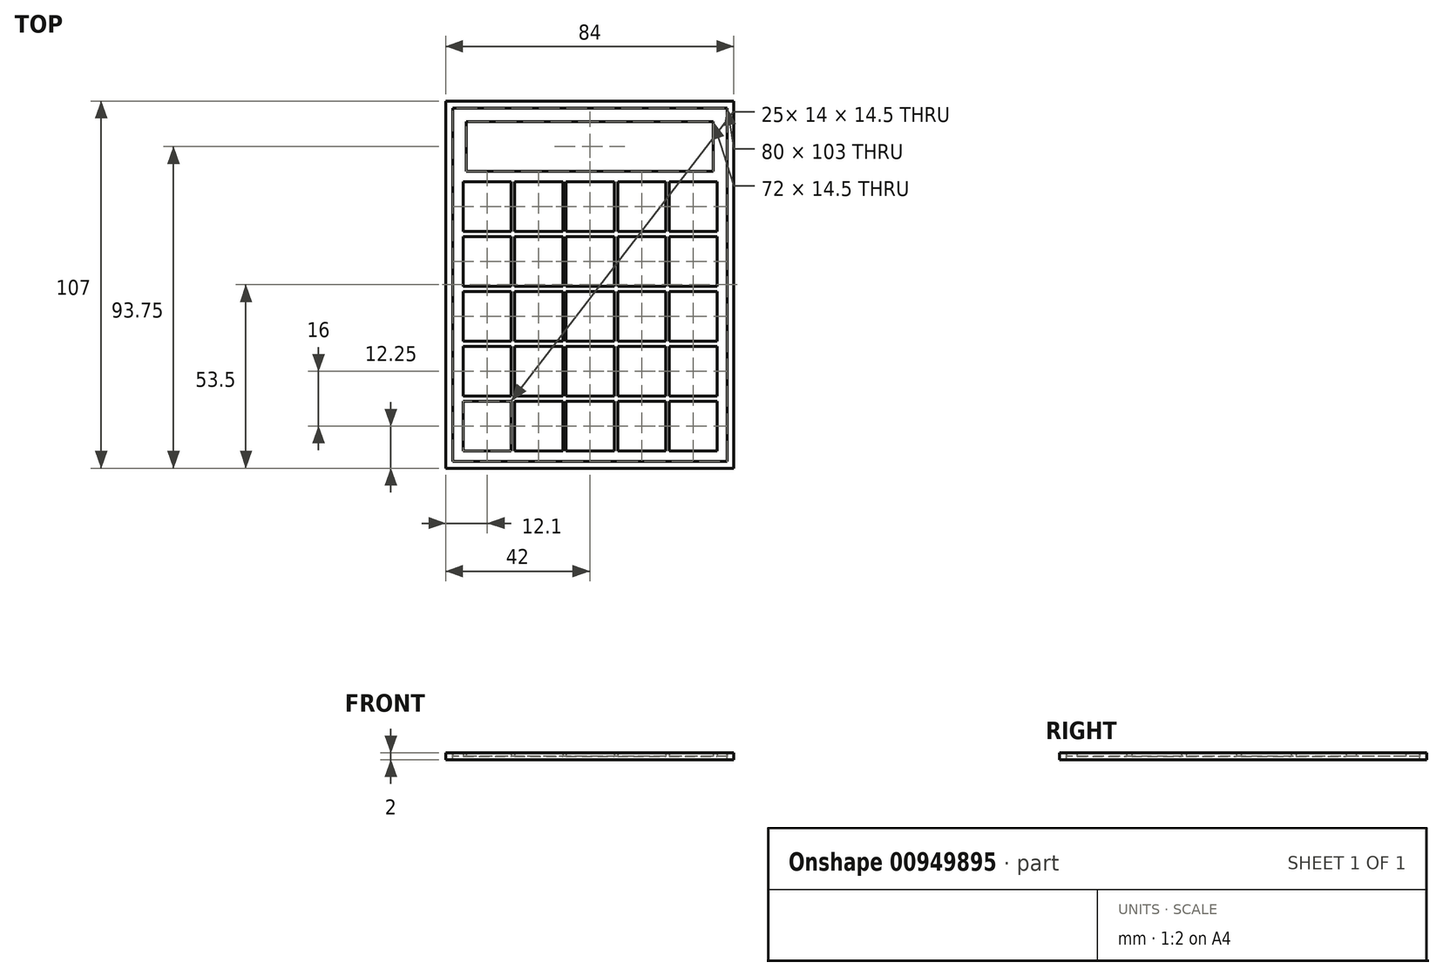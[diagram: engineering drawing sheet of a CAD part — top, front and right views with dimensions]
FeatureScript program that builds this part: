
annotation { "Feature Type Name" : "Feature", "Feature Type Description" : "" }
export const myFeature = defineFeature(function(context is Context, id is Id, definition is map)
    precondition{}
    {
        {
            var Q0;
            Q0=qCreatedBy(makeId("Top.planeOp"),FACE);
            var sketch = newSketch(context, id + "F0", { "sketchPlane" : qUnion([Q0])});
            skLineSegment(sketch, "E0.bottom", {"start": v(40, 51.5) * mm, "end": v(-40, 51.5) * mm});
            skLineSegment(sketch, "E0.top", {"start": v(40, -51.5) * mm, "end": v(-40, -51.5) * mm});
            skLineSegment(sketch, "E0.left", {"start": v(40, 51.5) * mm, "end": v(40, -51.5) * mm});
            skLineSegment(sketch, "E0.right", {"start": v(-40, 51.5) * mm, "end": v(-40, -51.5) * mm});
            skPoint(sketch, "E0.middle", {"position": v(0, 0) * mm});
            skLineSegment(sketch, "E1.bottom", {"start": v(-36.9, -48.5) * mm, "end": v(-22.9, -48.5) * mm});
            skLineSegment(sketch, "E1.top", {"start": v(-36.9, -34) * mm, "end": v(-22.9, -34) * mm});
            skLineSegment(sketch, "E1.left", {"start": v(-36.9, -48.5) * mm, "end": v(-36.9, -34) * mm});
            skLineSegment(sketch, "E1.right", {"start": v(-22.9, -48.5) * mm, "end": v(-22.9, -34) * mm});
            skLineSegment(sketch, "E2.0.1.0", {"start": v(-36.9, -32.5) * mm, "end": v(-36.9, -18) * mm});
            skLineSegment(sketch, "E2.0.1.1", {"start": v(-36.9, -18) * mm, "end": v(-22.9, -18) * mm});
            skLineSegment(sketch, "E2.0.1.2", {"start": v(-22.9, -32.5) * mm, "end": v(-22.9, -18) * mm});
            skLineSegment(sketch, "E2.0.1.3", {"start": v(-36.9, -32.5) * mm, "end": v(-22.9, -32.5) * mm});
            skLineSegment(sketch, "E2.0.2.0", {"start": v(-36.9, -16.5) * mm, "end": v(-36.9, -2) * mm});
            skLineSegment(sketch, "E2.0.2.1", {"start": v(-36.9, -2) * mm, "end": v(-22.9, -2) * mm});
            skLineSegment(sketch, "E2.0.2.2", {"start": v(-22.9, -16.5) * mm, "end": v(-22.9, -2) * mm});
            skLineSegment(sketch, "E2.0.2.3", {"start": v(-36.9, -16.5) * mm, "end": v(-22.9, -16.5) * mm});
            skLineSegment(sketch, "E2.0.3.0", {"start": v(-36.9, -0.5) * mm, "end": v(-36.9, 14) * mm});
            skLineSegment(sketch, "E2.0.3.1", {"start": v(-36.9, 14) * mm, "end": v(-22.9, 14) * mm});
            skLineSegment(sketch, "E2.0.3.2", {"start": v(-22.9, -0.5) * mm, "end": v(-22.9, 14) * mm});
            skLineSegment(sketch, "E2.0.3.3", {"start": v(-36.9, -0.5) * mm, "end": v(-22.9, -0.5) * mm});
            skLineSegment(sketch, "E2.0.4.0", {"start": v(-36.9, 15.5) * mm, "end": v(-36.9, 30) * mm});
            skLineSegment(sketch, "E2.0.4.1", {"start": v(-36.9, 30) * mm, "end": v(-22.9, 30) * mm});
            skLineSegment(sketch, "E2.0.4.2", {"start": v(-22.9, 15.5) * mm, "end": v(-22.9, 30) * mm});
            skLineSegment(sketch, "E2.0.4.3", {"start": v(-36.9, 15.5) * mm, "end": v(-22.9, 15.5) * mm});
            skLineSegment(sketch, "E2.1.0.0", {"start": v(-21.9, -48.5) * mm, "end": v(-21.9, -34) * mm});
            skLineSegment(sketch, "E2.1.0.1", {"start": v(-21.9, -34) * mm, "end": v(-7.9, -34) * mm});
            skLineSegment(sketch, "E2.1.0.2", {"start": v(-7.9, -48.5) * mm, "end": v(-7.9, -34) * mm});
            skLineSegment(sketch, "E2.1.0.3", {"start": v(-21.9, -48.5) * mm, "end": v(-7.9, -48.5) * mm});
            skLineSegment(sketch, "E2.1.1.0", {"start": v(-21.9, -32.5) * mm, "end": v(-21.9, -18) * mm});
            skLineSegment(sketch, "E2.1.1.1", {"start": v(-21.9, -18) * mm, "end": v(-7.9, -18) * mm});
            skLineSegment(sketch, "E2.1.1.2", {"start": v(-7.9, -32.5) * mm, "end": v(-7.9, -18) * mm});
            skLineSegment(sketch, "E2.1.1.3", {"start": v(-21.9, -32.5) * mm, "end": v(-7.9, -32.5) * mm});
            skLineSegment(sketch, "E2.1.2.0", {"start": v(-21.9, -16.5) * mm, "end": v(-21.9, -2) * mm});
            skLineSegment(sketch, "E2.1.2.1", {"start": v(-21.9, -2) * mm, "end": v(-7.9, -2) * mm});
            skLineSegment(sketch, "E2.1.2.2", {"start": v(-7.9, -16.5) * mm, "end": v(-7.9, -2) * mm});
            skLineSegment(sketch, "E2.1.2.3", {"start": v(-21.9, -16.5) * mm, "end": v(-7.9, -16.5) * mm});
            skLineSegment(sketch, "E2.1.3.0", {"start": v(-21.9, -0.5) * mm, "end": v(-21.9, 14) * mm});
            skLineSegment(sketch, "E2.1.3.1", {"start": v(-21.9, 14) * mm, "end": v(-7.9, 14) * mm});
            skLineSegment(sketch, "E2.1.3.2", {"start": v(-7.9, -0.5) * mm, "end": v(-7.9, 14) * mm});
            skLineSegment(sketch, "E2.1.3.3", {"start": v(-21.9, -0.5) * mm, "end": v(-7.9, -0.5) * mm});
            skLineSegment(sketch, "E2.1.4.0", {"start": v(-21.9, 15.5) * mm, "end": v(-21.9, 30) * mm});
            skLineSegment(sketch, "E2.1.4.1", {"start": v(-21.9, 30) * mm, "end": v(-7.9, 30) * mm});
            skLineSegment(sketch, "E2.1.4.2", {"start": v(-7.9, 15.5) * mm, "end": v(-7.9, 30) * mm});
            skLineSegment(sketch, "E2.1.4.3", {"start": v(-21.9, 15.5) * mm, "end": v(-7.9, 15.5) * mm});
            skLineSegment(sketch, "E2.2.0.0", {"start": v(-6.9, -48.5) * mm, "end": v(-6.9, -34) * mm});
            skLineSegment(sketch, "E2.2.0.1", {"start": v(-6.9, -34) * mm, "end": v(7.1, -34) * mm});
            skLineSegment(sketch, "E2.2.0.2", {"start": v(7.1, -48.5) * mm, "end": v(7.1, -34) * mm});
            skLineSegment(sketch, "E2.2.0.3", {"start": v(-6.9, -48.5) * mm, "end": v(7.1, -48.5) * mm});
            skLineSegment(sketch, "E2.2.1.0", {"start": v(-6.9, -32.5) * mm, "end": v(-6.9, -18) * mm});
            skLineSegment(sketch, "E2.2.1.1", {"start": v(-6.9, -18) * mm, "end": v(7.1, -18) * mm});
            skLineSegment(sketch, "E2.2.1.2", {"start": v(7.1, -32.5) * mm, "end": v(7.1, -18) * mm});
            skLineSegment(sketch, "E2.2.1.3", {"start": v(-6.9, -32.5) * mm, "end": v(7.1, -32.5) * mm});
            skLineSegment(sketch, "E2.2.2.0", {"start": v(-6.9, -16.5) * mm, "end": v(-6.9, -2) * mm});
            skLineSegment(sketch, "E2.2.2.1", {"start": v(-6.9, -2) * mm, "end": v(7.1, -2) * mm});
            skLineSegment(sketch, "E2.2.2.2", {"start": v(7.1, -16.5) * mm, "end": v(7.1, -2) * mm});
            skLineSegment(sketch, "E2.2.2.3", {"start": v(-6.9, -16.5) * mm, "end": v(7.1, -16.5) * mm});
            skLineSegment(sketch, "E2.2.3.0", {"start": v(-6.9, -0.5) * mm, "end": v(-6.9, 14) * mm});
            skLineSegment(sketch, "E2.2.3.1", {"start": v(-6.9, 14) * mm, "end": v(7.1, 14) * mm});
            skLineSegment(sketch, "E2.2.3.2", {"start": v(7.1, -0.5) * mm, "end": v(7.1, 14) * mm});
            skLineSegment(sketch, "E2.2.3.3", {"start": v(-6.9, -0.5) * mm, "end": v(7.1, -0.5) * mm});
            skLineSegment(sketch, "E2.2.4.0", {"start": v(-6.9, 15.5) * mm, "end": v(-6.9, 30) * mm});
            skLineSegment(sketch, "E2.2.4.1", {"start": v(-6.9, 30) * mm, "end": v(7.1, 30) * mm});
            skLineSegment(sketch, "E2.2.4.2", {"start": v(7.1, 15.5) * mm, "end": v(7.1, 30) * mm});
            skLineSegment(sketch, "E2.2.4.3", {"start": v(-6.9, 15.5) * mm, "end": v(7.1, 15.5) * mm});
            skLineSegment(sketch, "E2.3.0.0", {"start": v(8.1, -48.5) * mm, "end": v(8.1, -34) * mm});
            skLineSegment(sketch, "E2.3.0.1", {"start": v(8.1, -34) * mm, "end": v(22.1, -34) * mm});
            skLineSegment(sketch, "E2.3.0.2", {"start": v(22.1, -48.5) * mm, "end": v(22.1, -34) * mm});
            skLineSegment(sketch, "E2.3.0.3", {"start": v(8.1, -48.5) * mm, "end": v(22.1, -48.5) * mm});
            skLineSegment(sketch, "E2.3.1.0", {"start": v(8.1, -32.5) * mm, "end": v(8.1, -18) * mm});
            skLineSegment(sketch, "E2.3.1.1", {"start": v(8.1, -18) * mm, "end": v(22.1, -18) * mm});
            skLineSegment(sketch, "E2.3.1.2", {"start": v(22.1, -32.5) * mm, "end": v(22.1, -18) * mm});
            skLineSegment(sketch, "E2.3.1.3", {"start": v(8.1, -32.5) * mm, "end": v(22.1, -32.5) * mm});
            skLineSegment(sketch, "E2.3.2.0", {"start": v(8.1, -16.5) * mm, "end": v(8.1, -2) * mm});
            skLineSegment(sketch, "E2.3.2.1", {"start": v(8.1, -2) * mm, "end": v(22.1, -2) * mm});
            skLineSegment(sketch, "E2.3.2.2", {"start": v(22.1, -16.5) * mm, "end": v(22.1, -2) * mm});
            skLineSegment(sketch, "E2.3.2.3", {"start": v(8.1, -16.5) * mm, "end": v(22.1, -16.5) * mm});
            skLineSegment(sketch, "E2.3.3.0", {"start": v(8.1, -0.5) * mm, "end": v(8.1, 14) * mm});
            skLineSegment(sketch, "E2.3.3.1", {"start": v(8.1, 14) * mm, "end": v(22.1, 14) * mm});
            skLineSegment(sketch, "E2.3.3.2", {"start": v(22.1, -0.5) * mm, "end": v(22.1, 14) * mm});
            skLineSegment(sketch, "E2.3.3.3", {"start": v(8.1, -0.5) * mm, "end": v(22.1, -0.5) * mm});
            skLineSegment(sketch, "E2.3.4.0", {"start": v(8.1, 15.5) * mm, "end": v(8.1, 30) * mm});
            skLineSegment(sketch, "E2.3.4.1", {"start": v(8.1, 30) * mm, "end": v(22.1, 30) * mm});
            skLineSegment(sketch, "E2.3.4.2", {"start": v(22.1, 15.5) * mm, "end": v(22.1, 30) * mm});
            skLineSegment(sketch, "E2.3.4.3", {"start": v(8.1, 15.5) * mm, "end": v(22.1, 15.5) * mm});
            skLineSegment(sketch, "E2.4.0.0", {"start": v(23.1, -48.5) * mm, "end": v(23.1, -34) * mm});
            skLineSegment(sketch, "E2.4.0.1", {"start": v(23.1, -34) * mm, "end": v(37.1, -34) * mm});
            skLineSegment(sketch, "E2.4.0.2", {"start": v(37.1, -48.5) * mm, "end": v(37.1, -34) * mm});
            skLineSegment(sketch, "E2.4.0.3", {"start": v(23.1, -48.5) * mm, "end": v(37.1, -48.5) * mm});
            skLineSegment(sketch, "E2.4.1.0", {"start": v(23.1, -32.5) * mm, "end": v(23.1, -18) * mm});
            skLineSegment(sketch, "E2.4.1.1", {"start": v(23.1, -18) * mm, "end": v(37.1, -18) * mm});
            skLineSegment(sketch, "E2.4.1.2", {"start": v(37.1, -32.5) * mm, "end": v(37.1, -18) * mm});
            skLineSegment(sketch, "E2.4.1.3", {"start": v(23.1, -32.5) * mm, "end": v(37.1, -32.5) * mm});
            skLineSegment(sketch, "E2.4.2.0", {"start": v(23.1, -16.5) * mm, "end": v(23.1, -2) * mm});
            skLineSegment(sketch, "E2.4.2.1", {"start": v(23.1, -2) * mm, "end": v(37.1, -2) * mm});
            skLineSegment(sketch, "E2.4.2.2", {"start": v(37.1, -16.5) * mm, "end": v(37.1, -2) * mm});
            skLineSegment(sketch, "E2.4.2.3", {"start": v(23.1, -16.5) * mm, "end": v(37.1, -16.5) * mm});
            skLineSegment(sketch, "E2.4.3.0", {"start": v(23.1, -0.5) * mm, "end": v(23.1, 14) * mm});
            skLineSegment(sketch, "E2.4.3.1", {"start": v(23.1, 14) * mm, "end": v(37.1, 14) * mm});
            skLineSegment(sketch, "E2.4.3.2", {"start": v(37.1, -0.5) * mm, "end": v(37.1, 14) * mm});
            skLineSegment(sketch, "E2.4.3.3", {"start": v(23.1, -0.5) * mm, "end": v(37.1, -0.5) * mm});
            skLineSegment(sketch, "E2.4.4.0", {"start": v(23.1, 15.5) * mm, "end": v(23.1, 30) * mm});
            skLineSegment(sketch, "E2.4.4.1", {"start": v(23.1, 30) * mm, "end": v(37.1, 30) * mm});
            skLineSegment(sketch, "E2.4.4.2", {"start": v(37.1, 15.5) * mm, "end": v(37.1, 30) * mm});
            skLineSegment(sketch, "E2.4.4.3", {"start": v(23.1, 15.5) * mm, "end": v(37.1, 15.5) * mm});
            skLineSegment(sketch, "E2.direction1", {"start": v(-36.9, -48.5) * mm, "end": v(-21.9, -48.5) * mm, "construction": true});
            skLineSegment(sketch, "E2.direction2", {"start": v(-36.9, -48.5) * mm, "end": v(-36.9, -32.5) * mm, "construction": true});
            skLineSegment(sketch, "E3.bottom", {"start": v(36, 47.5) * mm, "end": v(-36, 47.5) * mm});
            skLineSegment(sketch, "E3.top", {"start": v(36, 33) * mm, "end": v(-36, 33) * mm});
            skLineSegment(sketch, "E3.left", {"start": v(36, 47.5) * mm, "end": v(36, 33) * mm});
            skLineSegment(sketch, "E3.right", {"start": v(-36, 47.5) * mm, "end": v(-36, 33) * mm});
            skPoint(sketch, "E3.middle", {"position": v(0, 40.25) * mm});
            skSolve(sketch);
        }
        {
            var Q0;
            Q0=makeQuery(id+"F0.imprint","IMPRINT",FACE,{"disambiguationData":[TD([[makeQuery(id+"F0.imprint","IMPRINT",EDGE,{"derivedFrom":sQuery(id+"F0.wireOp",EDGE,"E0.bottom")}),1.0]])]});
            extrude(context, id + "F1", {"entities" : qUnion([Q0]), "depth" : 1 * mm, "offsetDistance" : 25 * mm});
        }
        {
            var Q0;
            Q0=makeQuery(id+"F1.opExtrude","CAP_FACE",FACE,{"disambiguationData":[OSD([sQuery(id+"F0.wireOp",EDGE,"E0.bottom"),sQuery(id+"F0.wireOp",EDGE,"E0.top"),sQuery(id+"F0.wireOp",EDGE,"E0.left"),sQuery(id+"F0.wireOp",EDGE,"E0.right"),sQuery(id+"F0.wireOp",EDGE,"E1.bottom"),sQuery(id+"F0.wireOp",EDGE,"E1.top"),sQuery(id+"F0.wireOp",EDGE,"E1.left"),sQuery(id+"F0.wireOp",EDGE,"E1.right"),sQuery(id+"F0.wireOp",EDGE,"E2.0.1.0"),sQuery(id+"F0.wireOp",EDGE,"E2.0.1.1"),sQuery(id+"F0.wireOp",EDGE,"E2.0.1.2"),sQuery(id+"F0.wireOp",EDGE,"E2.0.1.3"),sQuery(id+"F0.wireOp",EDGE,"E2.0.2.0"),sQuery(id+"F0.wireOp",EDGE,"E2.0.2.1"),sQuery(id+"F0.wireOp",EDGE,"E2.0.2.2"),sQuery(id+"F0.wireOp",EDGE,"E2.0.2.3"),sQuery(id+"F0.wireOp",EDGE,"E2.0.3.0"),sQuery(id+"F0.wireOp",EDGE,"E2.0.3.1"),sQuery(id+"F0.wireOp",EDGE,"E2.0.3.2"),sQuery(id+"F0.wireOp",EDGE,"E2.0.3.3"),sQuery(id+"F0.wireOp",EDGE,"E2.0.4.0"),sQuery(id+"F0.wireOp",EDGE,"E2.0.4.1"),sQuery(id+"F0.wireOp",EDGE,"E2.0.4.2"),sQuery(id+"F0.wireOp",EDGE,"E2.0.4.3"),sQuery(id+"F0.wireOp",EDGE,"E2.1.0.0"),sQuery(id+"F0.wireOp",EDGE,"E2.1.0.1"),sQuery(id+"F0.wireOp",EDGE,"E2.1.0.2"),sQuery(id+"F0.wireOp",EDGE,"E2.1.0.3"),sQuery(id+"F0.wireOp",EDGE,"E2.1.1.0"),sQuery(id+"F0.wireOp",EDGE,"E2.1.1.1"),sQuery(id+"F0.wireOp",EDGE,"E2.1.1.2"),sQuery(id+"F0.wireOp",EDGE,"E2.1.1.3"),sQuery(id+"F0.wireOp",EDGE,"E2.1.2.0"),sQuery(id+"F0.wireOp",EDGE,"E2.1.2.1"),sQuery(id+"F0.wireOp",EDGE,"E2.1.2.2"),sQuery(id+"F0.wireOp",EDGE,"E2.1.2.3"),sQuery(id+"F0.wireOp",EDGE,"E2.1.3.0"),sQuery(id+"F0.wireOp",EDGE,"E2.1.3.1"),sQuery(id+"F0.wireOp",EDGE,"E2.1.3.2"),sQuery(id+"F0.wireOp",EDGE,"E2.1.3.3"),sQuery(id+"F0.wireOp",EDGE,"E2.1.4.0"),sQuery(id+"F0.wireOp",EDGE,"E2.1.4.1"),sQuery(id+"F0.wireOp",EDGE,"E2.1.4.2"),sQuery(id+"F0.wireOp",EDGE,"E2.1.4.3"),sQuery(id+"F0.wireOp",EDGE,"E2.2.0.0"),sQuery(id+"F0.wireOp",EDGE,"E2.2.0.1"),sQuery(id+"F0.wireOp",EDGE,"E2.2.0.2"),sQuery(id+"F0.wireOp",EDGE,"E2.2.0.3"),sQuery(id+"F0.wireOp",EDGE,"E2.2.1.0"),sQuery(id+"F0.wireOp",EDGE,"E2.2.1.1"),sQuery(id+"F0.wireOp",EDGE,"E2.2.1.2"),sQuery(id+"F0.wireOp",EDGE,"E2.2.1.3"),sQuery(id+"F0.wireOp",EDGE,"E2.2.2.0"),sQuery(id+"F0.wireOp",EDGE,"E2.2.2.1"),sQuery(id+"F0.wireOp",EDGE,"E2.2.2.2"),sQuery(id+"F0.wireOp",EDGE,"E2.2.2.3"),sQuery(id+"F0.wireOp",EDGE,"E2.2.3.0"),sQuery(id+"F0.wireOp",EDGE,"E2.2.3.1"),sQuery(id+"F0.wireOp",EDGE,"E2.2.3.2"),sQuery(id+"F0.wireOp",EDGE,"E2.2.3.3"),sQuery(id+"F0.wireOp",EDGE,"E2.2.4.0"),sQuery(id+"F0.wireOp",EDGE,"E2.2.4.1"),sQuery(id+"F0.wireOp",EDGE,"E2.2.4.2"),sQuery(id+"F0.wireOp",EDGE,"E2.2.4.3"),sQuery(id+"F0.wireOp",EDGE,"E2.3.0.0"),sQuery(id+"F0.wireOp",EDGE,"E2.3.0.1"),sQuery(id+"F0.wireOp",EDGE,"E2.3.0.2"),sQuery(id+"F0.wireOp",EDGE,"E2.3.0.3"),sQuery(id+"F0.wireOp",EDGE,"E2.3.1.0"),sQuery(id+"F0.wireOp",EDGE,"E2.3.1.1"),sQuery(id+"F0.wireOp",EDGE,"E2.3.1.2"),sQuery(id+"F0.wireOp",EDGE,"E2.3.1.3"),sQuery(id+"F0.wireOp",EDGE,"E2.3.2.0"),sQuery(id+"F0.wireOp",EDGE,"E2.3.2.1"),sQuery(id+"F0.wireOp",EDGE,"E2.3.2.2"),sQuery(id+"F0.wireOp",EDGE,"E2.3.2.3"),sQuery(id+"F0.wireOp",EDGE,"E2.3.3.0"),sQuery(id+"F0.wireOp",EDGE,"E2.3.3.1"),sQuery(id+"F0.wireOp",EDGE,"E2.3.3.2"),sQuery(id+"F0.wireOp",EDGE,"E2.3.3.3"),sQuery(id+"F0.wireOp",EDGE,"E2.3.4.0"),sQuery(id+"F0.wireOp",EDGE,"E2.3.4.1"),sQuery(id+"F0.wireOp",EDGE,"E2.3.4.2"),sQuery(id+"F0.wireOp",EDGE,"E2.3.4.3"),sQuery(id+"F0.wireOp",EDGE,"E2.4.0.0"),sQuery(id+"F0.wireOp",EDGE,"E2.4.0.1"),sQuery(id+"F0.wireOp",EDGE,"E2.4.0.2"),sQuery(id+"F0.wireOp",EDGE,"E2.4.0.3"),sQuery(id+"F0.wireOp",EDGE,"E2.4.1.0"),sQuery(id+"F0.wireOp",EDGE,"E2.4.1.1"),sQuery(id+"F0.wireOp",EDGE,"E2.4.1.2"),sQuery(id+"F0.wireOp",EDGE,"E2.4.1.3"),sQuery(id+"F0.wireOp",EDGE,"E2.4.2.0"),sQuery(id+"F0.wireOp",EDGE,"E2.4.2.1"),sQuery(id+"F0.wireOp",EDGE,"E2.4.2.2"),sQuery(id+"F0.wireOp",EDGE,"E2.4.2.3"),sQuery(id+"F0.wireOp",EDGE,"E2.4.3.0"),sQuery(id+"F0.wireOp",EDGE,"E2.4.3.1"),sQuery(id+"F0.wireOp",EDGE,"E2.4.3.2"),sQuery(id+"F0.wireOp",EDGE,"E2.4.3.3"),sQuery(id+"F0.wireOp",EDGE,"E2.4.4.0"),sQuery(id+"F0.wireOp",EDGE,"E2.4.4.1"),sQuery(id+"F0.wireOp",EDGE,"E2.4.4.2"),sQuery(id+"F0.wireOp",EDGE,"E2.4.4.3"),sQuery(id+"F0.wireOp",EDGE,"E3.bottom"),sQuery(id+"F0.wireOp",EDGE,"E3.top"),sQuery(id+"F0.wireOp",EDGE,"E3.left"),sQuery(id+"F0.wireOp",EDGE,"E3.right")])],"isStart":false});
            var sketch = newSketch(context, id + "F2", { "sketchPlane" : qUnion([Q0])});
            skLineSegment(sketch, "E4.bottom", {"start": v(-40, -51.5) * mm, "end": v(-42, -51.5) * mm});
            skLineSegment(sketch, "E4.top", {"start": v(-40, 53.5) * mm, "end": v(-42, 53.5) * mm});
            skLineSegment(sketch, "E4.left", {"start": v(-40, -51.5) * mm, "end": v(-40, 53.5) * mm});
            skLineSegment(sketch, "E4.right", {"start": v(-42, -51.5) * mm, "end": v(-42, 53.5) * mm});
            skLineSegment(sketch, "E5.bottom", {"start": v(-40, 53.5) * mm, "end": v(0, 53.5) * mm});
            skLineSegment(sketch, "E5.top", {"start": v(-40, 51.5) * mm, "end": v(0, 51.5) * mm});
            skLineSegment(sketch, "E5.left", {"start": v(-40, 53.5) * mm, "end": v(-40, 51.5) * mm});
            skLineSegment(sketch, "E5.right", {"start": v(0, 53.5) * mm, "end": v(0, 51.5) * mm});
            skLineSegment(sketch, "E6.MirrorCS", {"start": v(40, 53.5) * mm, "end": v(0, 53.5) * mm});
            skLineSegment(sketch, "E7.MirrorCS", {"start": v(40, 51.5) * mm, "end": v(0, 51.5) * mm});
            skLineSegment(sketch, "E8.MirrorCS", {"start": v(42, -51.5) * mm, "end": v(42, 53.5) * mm});
            skLineSegment(sketch, "E9.MirrorCS", {"start": v(40, -51.5) * mm, "end": v(40, 53.5) * mm});
            skLineSegment(sketch, "E10.MirrorCS", {"start": v(40, -51.5) * mm, "end": v(42, -51.5) * mm});
            skLineSegment(sketch, "E11.MirrorCS", {"start": v(40, 53.5) * mm, "end": v(42, 53.5) * mm});
            skLineSegment(sketch, "E12.bottom", {"start": v(-42, -51.5) * mm, "end": v(0, -51.5) * mm});
            skLineSegment(sketch, "E12.top", {"start": v(-42, -53.5) * mm, "end": v(0, -53.5) * mm});
            skLineSegment(sketch, "E12.left", {"start": v(-42, -51.5) * mm, "end": v(-42, -53.5) * mm});
            skLineSegment(sketch, "E12.right", {"start": v(0, -51.5) * mm, "end": v(0, -53.5) * mm});
            skLineSegment(sketch, "E13.MirrorCS", {"start": v(42, -51.5) * mm, "end": v(42, -53.5) * mm});
            skLineSegment(sketch, "E14.MirrorCS", {"start": v(42, -51.5) * mm, "end": v(0, -51.5) * mm});
            skLineSegment(sketch, "E15.MirrorCS", {"start": v(42, -53.5) * mm, "end": v(0, -53.5) * mm});
            skSolve(sketch);
        }
        {
            var Q0;
            Q0=makeQuery(id+"F2.imprint","IMPRINT",FACE,{"disambiguationData":[TD([[makeQuery(id+"F2.imprint","IMPRINT",EDGE,{"derivedFrom":sQuery(id+"F2.wireOp",EDGE,"E12.top")}),1.0]])]});
            var Q1;
            {var subQ3=sQuery(id+"F2.wireOp",EDGE,"E12.right");Q1=makeQuery(id+"F2.imprint","IMPRINT",FACE,{"disambiguationData":[TD([[makeQuery(id+"F2.imprint","IMPRINT",EDGE,{"derivedFrom":subQ3}),1.0]])]});}
            var Q2;
            {var subQ5=sQuery(id+"F2.wireOp",EDGE,"E8.MirrorCS");Q2=makeQuery(id+"F2.imprint","IMPRINT",FACE,{"disambiguationData":[TD([[makeQuery(id+"F2.imprint","IMPRINT",EDGE,{"derivedFrom":subQ5}),1.0]])]});}
            var Q3;
            Q3=makeQuery(id+"F2.imprint","IMPRINT",FACE,{"disambiguationData":[TD([[makeQuery(id+"F2.imprint","IMPRINT",EDGE,{"derivedFrom":sQuery(id+"F2.wireOp",EDGE,"E4.top")}),1.0]])]});
            var Q4;
            Q4=makeQuery(id+"F2.imprint","IMPRINT",FACE,{"disambiguationData":[TD([[makeQuery(id+"F2.imprint","IMPRINT",EDGE,{"derivedFrom":sQuery(id+"F2.wireOp",EDGE,"E5.bottom")}),-1.0]])]});
            var Q5;
            Q5=makeQuery(id+"F2.imprint","IMPRINT",FACE,{"disambiguationData":[TD([[makeQuery(id+"F2.imprint","IMPRINT",EDGE,{"derivedFrom":sQuery(id+"F2.wireOp",EDGE,"E5.right")}),1.0]])]});
            extrude(context, id + "F3", {"entities" : qUnion([Q0, Q1, Q2, Q3, Q4, Q5]), "oppositeDirection" : true, "depth" : 2 * mm, "offsetDistance" : 25 * mm});
        }
    });
